# Revit family: Gira_531900
name_source: partatom
category: Elektroinstallationen
revit_build: Autodesk Revit 2017 (Build: 20160225_1515(x64)
units: mm (PartAtom-declared; Revit-internal decimal feet)

## family parameters
Basisbauteil = Fläche
Beim Laden mit Abzugskörper schneiden = Nein
Bemaßung runder Anschluss = Durchmesser verwenden
Beschriftungsausrichtung beibehalten = Nein
Gemeinsam genutzt = Nein
Raumberechnungspunkt = Nein
Teiletyp = Normal

## types (1)
- Spannungsversorgung DC 12 V 2 A REG Zubehör
    Andere Bussysteme = eNet
    BIM = https://media.stage.bim.site 2f.rfa
    BIMSITE_PRODUCT_ID = d6225ded82d3066a22a992929dfc11803a763672
    Beschreibung = Spannungsversorgung DC 12 V 2 A  REG Merkmale:  Spannungsversorgung DC 12 V für den eNet Server, eNet Funk Empfangsmodul und Externe Kamera.
    Breite in Teilungseinheiten = 2
    Bussystem Funkbus = Ja
    Bussystem KNX = Nein
    Bussystem KNX-Funk = Nein
    Bussystem LON = Nein
    Bussystem Powernet = Nein
    Datenblatt = https://media.stage.bim.site
    Datenblatt 1 = https://media.stage.bim.site
    GTIN = 4010337774037
    HAN = 531900
    HeinzeBIM = https://www.heinze.de
    Hersteller = Gira
    Kosten = 0 $
    Mit LED-Anzeige = Nein
    Montageart = REG
    Produktseite = https://media.stage.bim.site
    Typname = Spannungsversorgung DC 12 V 2 A REG Zubehör
    URL = https://www.gira.de
    Vorgabe-Ansicht = 1219 mm

## geometry (parser evidence)
native form markers: Sweep x3
no freeform markers — native parametric forms only
